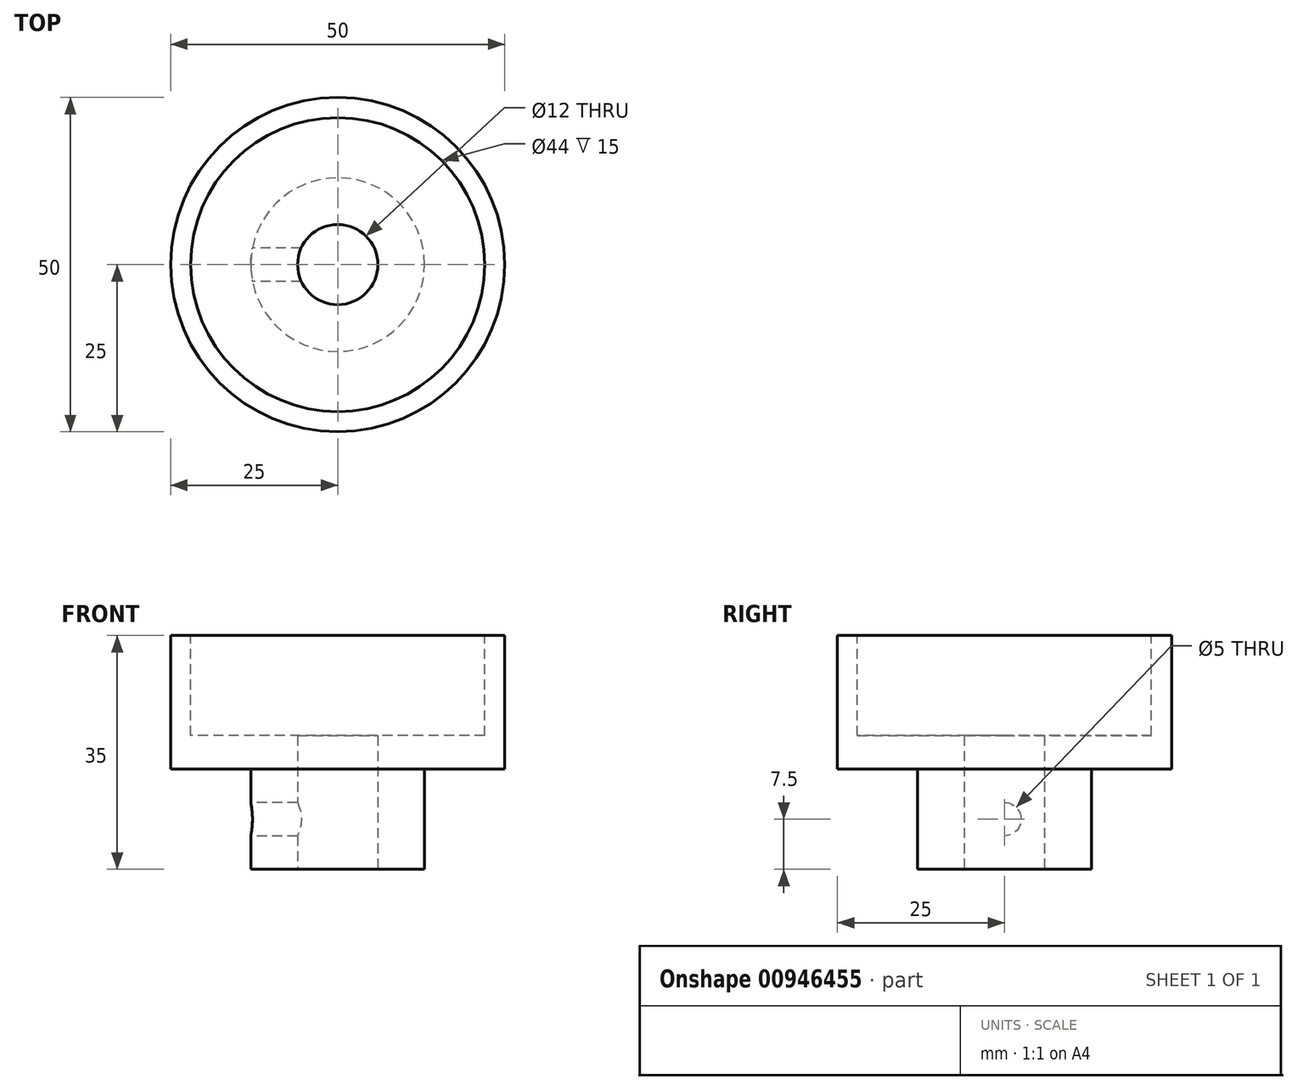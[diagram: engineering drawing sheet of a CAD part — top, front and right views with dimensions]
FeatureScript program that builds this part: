
annotation { "Feature Type Name" : "Feature", "Feature Type Description" : "" }
export const myFeature = defineFeature(function(context is Context, id is Id, definition is map)
    precondition{}
    {
        {
            var Q0;
            Q0=qCreatedBy(makeId("Top.planeOp"),FACE);
            var sketch = newSketch(context, id + "F0", { "sketchPlane" : qUnion([Q0])});
            skCircle(sketch, "E0", {"center": v(0, 0) * mm, "radius": 25 * mm});
            skSolve(sketch);
        }
        {
            var Q0;
            Q0 = qSketchRegion(id + "F0", true);
            extrude(context, id + "F1", {"entities" : qUnion([Q0]), "depth" : 20 * mm, "offsetDistance" : 25 * mm});
        }
        {
            var Q0;
            Q0=makeQuery(id+"F1.opExtrude","CAP_FACE",FACE,{"disambiguationData":[OSD([sQuery(id+"F0.wireOp",EDGE,"E0")])],"isStart":true});
            var sketch = newSketch(context, id + "F2", { "sketchPlane" : qUnion([Q0])});
            skCircle(sketch, "E1", {"center": v(0, 0) * mm, "radius": 13 * mm});
            skSolve(sketch);
        }
        {
            var Q0;
            Q0 = qSketchRegion(id + "F2", true);
            extrude(context, id + "F3", {"entities" : qUnion([Q0]), "operationType" : NewBodyOperationType.ADD, "depth" : 15 * mm, "offsetDistance" : 25 * mm});
        }
        {
            var Q0;
            Q0=makeQuery(id+"F1.opExtrude","CAP_FACE",FACE,{"disambiguationData":[OSD([sQuery(id+"F0.wireOp",EDGE,"E0")])],"isStart":false});
            var sketch = newSketch(context, id + "F4", { "sketchPlane" : qUnion([Q0])});
            skCircle(sketch, "E2", {"center": v(0, 0) * mm, "radius": 22 * mm});
            skSolve(sketch);
        }
        {
            var Q0;
            Q0 = qSketchRegion(id + "F4", true);
            extrude(context, id + "F5", {"entities" : qUnion([Q0]), "operationType" : NewBodyOperationType.REMOVE, "oppositeDirection" : true, "depth" : 15 * mm, "offsetDistance" : 25 * mm});
        }
        {
            var Q0;
            Q0=makeQuery(id+"F3.opExtrude","CAP_FACE",FACE,{"disambiguationData":[OSD([sQuery(id+"F2.wireOp",EDGE,"E1")])],"isStart":false});
            var sketch = newSketch(context, id + "F6", { "sketchPlane" : qUnion([Q0])});
            skCircle(sketch, "E3", {"center": v(0, 0) * mm, "radius": 6 * mm});
            skSolve(sketch);
        }
        {
            var Q0;
            Q0 = qSketchRegion(id + "F6", true);
            extrude(context, id + "F7", {"entities" : qUnion([Q0]), "operationType" : NewBodyOperationType.REMOVE, "endBound" : BoundingType.THROUGH_ALL, "oppositeDirection" : true, "depth" : 25 * mm, "offsetDistance" : 25 * mm});
        }
        {
            var Q0;
            Q0=qCreatedBy(makeId("Right.planeOp"),FACE);
            cPlane(context, id + "F8", {"entities" : qUnion([Q0]), "cplaneType" : CPlaneType.OFFSET, "offset" : 25 * mm, "oppositeDirection" : true, "width" : 150 * mm, "height" : 150 * mm});
        }
        {
            var Q0;
            Q0=qCreatedBy(id+"F8.planeOp",FACE);
            var sketch = newSketch(context, id + "F9", { "sketchPlane" : qUnion([Q0])});
            skCircle(sketch, "E4", {"center": v(0, -7.5) * mm, "radius": 2.5 * mm});
            skSolve(sketch);
        }
        {
            var Q0;
            Q0 = qSketchRegion(id + "F9", true);
            extrude(context, id + "F10", {"entities" : qUnion([Q0]), "operationType" : NewBodyOperationType.REMOVE, "depth" : 25 * mm, "offsetDistance" : 25 * mm});
        }
    });
